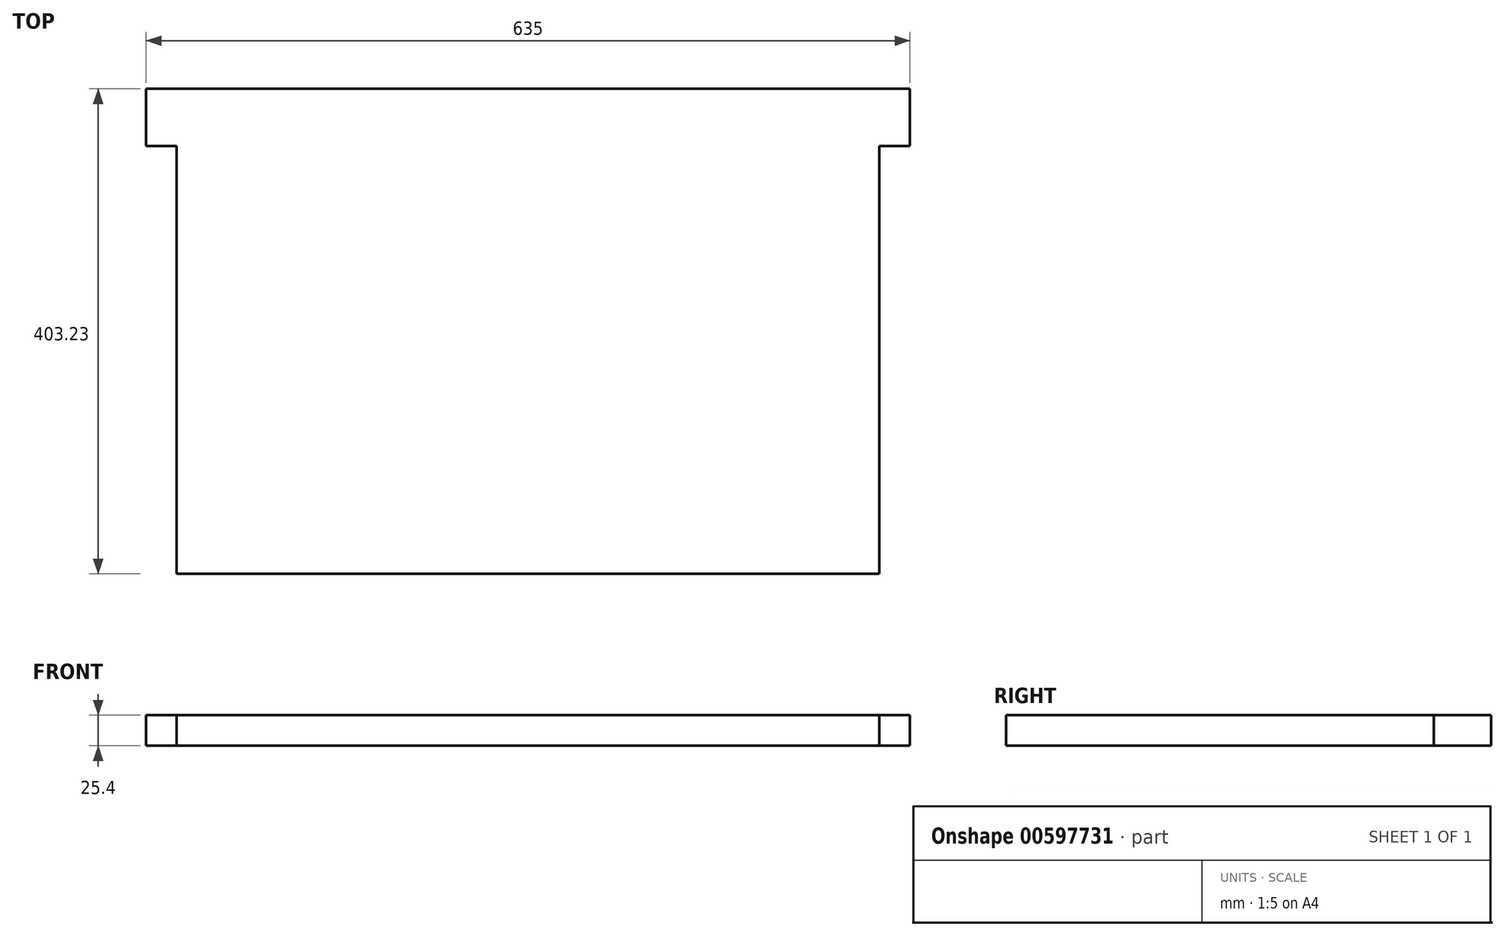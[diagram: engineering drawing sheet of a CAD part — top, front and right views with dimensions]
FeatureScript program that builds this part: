
annotation { "Feature Type Name" : "Feature", "Feature Type Description" : "" }
export const myFeature = defineFeature(function(context is Context, id is Id, definition is map)
    precondition{}
    {
        {
            var Q0;
            Q0=qCreatedBy(makeId("Top.planeOp"),FACE);
            var sketch = newSketch(context, id + "F0", { "sketchPlane" : qUnion([Q0])});
            skLineSegment(sketch, "E0.bottom", {"start": v(-635, 403.23) * mm, "end": v(0, 403.23) * mm});
            skLineSegment(sketch, "E0.top", {"start": v(-635, 0) * mm, "end": v(0, 0) * mm});
            skLineSegment(sketch, "E0.left", {"start": v(-635, 403.23) * mm, "end": v(-635, 0) * mm});
            skLineSegment(sketch, "E0.right", {"start": v(0, 403.23) * mm, "end": v(0, 0) * mm});
            skSolve(sketch);
        }
        {
            var Q0;
            Q0 = qSketchRegion(id + "F0", true);
            extrude(context, id + "F1", {"entities" : qUnion([Q0]), "depth" : 25.4 * mm, "offsetDistance" : 25.4 * mm});
        }
        {
            var Q0;
            Q0=makeQuery(id+"F1.opExtrude","CAP_FACE",FACE,{"disambiguationData":[OSD([sQuery(id+"F0.wireOp",EDGE,"E0.bottom"),sQuery(id+"F0.wireOp",EDGE,"E0.top"),sQuery(id+"F0.wireOp",EDGE,"E0.left"),sQuery(id+"F0.wireOp",EDGE,"E0.right")])],"isStart":true});
            var sketch = newSketch(context, id + "F2", { "sketchPlane" : qUnion([Q0])});
            skLineSegment(sketch, "E1.bottom", {"start": v(0, 0) * mm, "end": v(-25.4, 0) * mm});
            skLineSegment(sketch, "E1.top", {"start": v(0, -355.6) * mm, "end": v(-25.4, -355.6) * mm});
            skLineSegment(sketch, "E1.left", {"start": v(0, 0) * mm, "end": v(0, -355.6) * mm});
            skLineSegment(sketch, "E1.right", {"start": v(-25.4, 0) * mm, "end": v(-25.4, -355.6) * mm});
            skLineSegment(sketch, "E2.bottom", {"start": v(-635, 0) * mm, "end": v(-609.6, 0) * mm});
            skLineSegment(sketch, "E2.top", {"start": v(-635, -355.6) * mm, "end": v(-609.6, -355.6) * mm});
            skLineSegment(sketch, "E2.left", {"start": v(-635, 0) * mm, "end": v(-635, -355.6) * mm});
            skLineSegment(sketch, "E2.right", {"start": v(-609.6, 0) * mm, "end": v(-609.6, -355.6) * mm});
            skSolve(sketch);
        }
        {
            var Q0;
            Q0 = qSketchRegion(id + "F2", true);
            extrude(context, id + "F3", {"entities" : qUnion([Q0]), "operationType" : NewBodyOperationType.REMOVE, "endBound" : BoundingType.UP_TO_NEXT, "oppositeDirection" : true, "depth" : 25.4 * mm, "offsetDistance" : 25.4 * mm});
        }
    });
